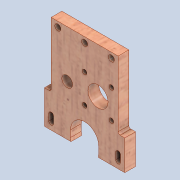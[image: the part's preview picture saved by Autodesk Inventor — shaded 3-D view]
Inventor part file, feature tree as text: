
AUTODESK INVENTOR PART (.ipt)
format: ipt  version: 2020 (Build 240168000, 168)  size: 298,496 bytes
history: native  units: mm
features: extrude x6, sketch x4, other x3, direct_edit x1, hole x1, fillet x1, reference x1, move_body x1
ambient origin geometry x8: Origin, YZ Plane, XZ Plane, XY Plane, X Axis, Y Axis, Z Axis, Center Point
bodies: Solid1 (feature_tree)
feature tree (18):
  extrude  "Extrusion1"  Depth=60.0mm
  extrude  "Extrusion4"  Depth=10.0mm TaperAngle=0.0deg
  extrude  "Extrusion5"  TaperAngle=0.0deg  [1 undecoded]
  extrude  "Extrusion6"  Depth=5.0mm
  extrude  "Extrusion7"  Depth=5.0mm
  extrude  "Extrusion8"  TaperAngle=0.0deg  [1 undecoded]
  direct_edit  "Direct Edit1"
  hole  "Hole1"  [1 undecoded]
  fillet  "Fillet1"  Radius=3.5mm
  sketch  "Sketch1"  dims[d0=60.0mm d1=65.0mm]
  sketch  "Sketch7"  dims[d2=8.0mm d3=0.0mm d11=10.0mm d12=0.0mm]
  reference  "Reference6"
  sketch  "Sketch8"  dims[d13=15.0mm d14=0.0mm d15=0.0mm]
  sketch  "Sketch9"  dims[d16=0.0mm d17=0.0mm d18=5.0mm d19=5.0mm d20=0.0mm d21=0.0mm d22=5.0mm d23=3.5mm d24=5.0mm d25=10.5mm d26=7.5mm d27=30.0mm d28=25.608627mm d29=20.0mm d31=21.5mm d33=3.5mm d35=8.0mm d36=17.0mm d37=27.469095mm d38=10.0mm d39=0.0mm d42=20.0mm d43=40.0mm d44=0.0mm d45=0.0mm d46=8.0mm d47=20.0mm d48=20.0mm d49=4.0mm d50=4.5mm d51=6.0mm d52=4.0mm d53=2.0mm d54=90.0deg d55=8.0mm d56=20.594885mm d57=1.5mm]
  parser-record x1  (decoder bookkeeping rows leaked as tree rows — omitted from the tree; the rows remain in map.json)
  other  "0005-00-00 Ansamblu_General.iam"
  other  "0005-10-002 Suport1 Seringa.ipt:8"
  move_body  "Move1"
note: 3 required parameter values undecoded (feature->parameter linkage not recoverable at this tier; creation-order binding heuristic only, values carry confidence <= 0.55)
note: 1 file-system path scrubbed to <path> (originals preserved in map.json)
